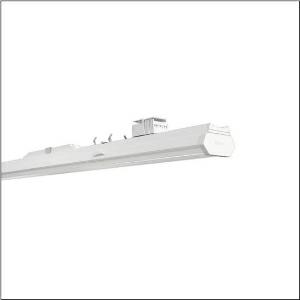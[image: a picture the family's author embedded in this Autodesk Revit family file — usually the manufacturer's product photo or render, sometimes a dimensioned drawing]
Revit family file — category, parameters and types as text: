
# Revit family: licross_r__21_protected_mo_52td1bvn455g_6e17
name_source: partatom
category: Lighting Fixtures
units: mm (PartAtom-declared; Revit-internal decimal feet)

## family parameters
Cut with Voids When Loaded = No
Host = Face
Light Source = No
Part Type = Normal
Room Calculation Point = No
Round Connector Dimension = Use Diameter
Shared = No

## types (1)
- --- (1 x LED, 5500 lm, 32.3 W, 4000K)
    Apparent Load = 32 VA
    CIE Flux Codes = 54 82 95 97 100
    Color Rendering = 80
    Color Temperature = 4000K
    Default Elevation = 1800 mm
    Description = Licross® 21 Protected MO, luminaire insert, of sheet steel, galvanised, coil coated, white, length: 1.500mm, width: 90mm, height: 101mm, LED rated luminous flux: 5.500lm, light colour: 840, control gear: DALI 2, CLO, with plug, 5-pole, with phase selection, mains connection: 220..240V, AC, 50/60Hz, start of lifetime: 32W, end of service life: 38W, halogen-free wiring, primary optical cover: cover, of PMMA, light emission: direct distribution, primary light characteristic: symmetric, protection rating (complete): IP54, insulation class (complete): insulation class I (protective earthing), certification: CE, ENEC, VDE, UKCA, protection symbol: D if used in an environment with non-conductive dust loads with corresponding accessories, impact resistance: IK06, permissible ambient temperature for indoor applications: -25..+45°C, corresponds to IFS (International Featured Standards) requirements for safety and quality in the food industry, reducing of maximum allowable ambient temperature of 5°C with ceiling mounting, LABS conformity tested according to VDMA 24364:2018-05, packaging unit: 1 piece
    Height = 92 mm
    Lamp = 1 x LED
    Lamp Light Flux = 5500 lm
    Lamp Power = 32.3 W
    Lamp count = 1
    Length = 1500 mm
    Luminous efficacy = 170 lm/W
    Manufacturer = Siteco
    ModVariant = No
    Model = 52TD1BVN455G
    Mounting Place = Ceiling
    Mounting Type = Pendant
    Number of Poles = 1
    OnlyDefault = Yes
    Power Factor = 1
    Product Name = Licross® 21 Protected MO
    Product group = luminaire insert
    ProductGroupID = 902
    Protection Class = Protection class I
    Protection Degree = IP 54
    RLX_Detail_Level = 1
    RLX_Emergency_Light_Flux = 0 lm
    RLX_Emergency_Type = 0
    RLX_Emergency_Type_DB = No
    RlxData = <blob elided: 23961 chars, md5=0b9528d6>
    Socket = socket
    Standby Power = 0 W
    System Light Flux = 5500 lm
    System Power = 32 W
    Type Comments = factory setting: luminous flux: 100 % | dim-lin: 254 | 219 mA
    Type Image = l_1256148.jpg
    URL = http://relux.com
    VarID = @adj_082784
    Voltage = 0 V
    Weight = 0.00 kg
    Width = 88 mm

## geometry (parser evidence)
native form markers: Blend x4, Sweep x9
no freeform markers — native parametric forms only
